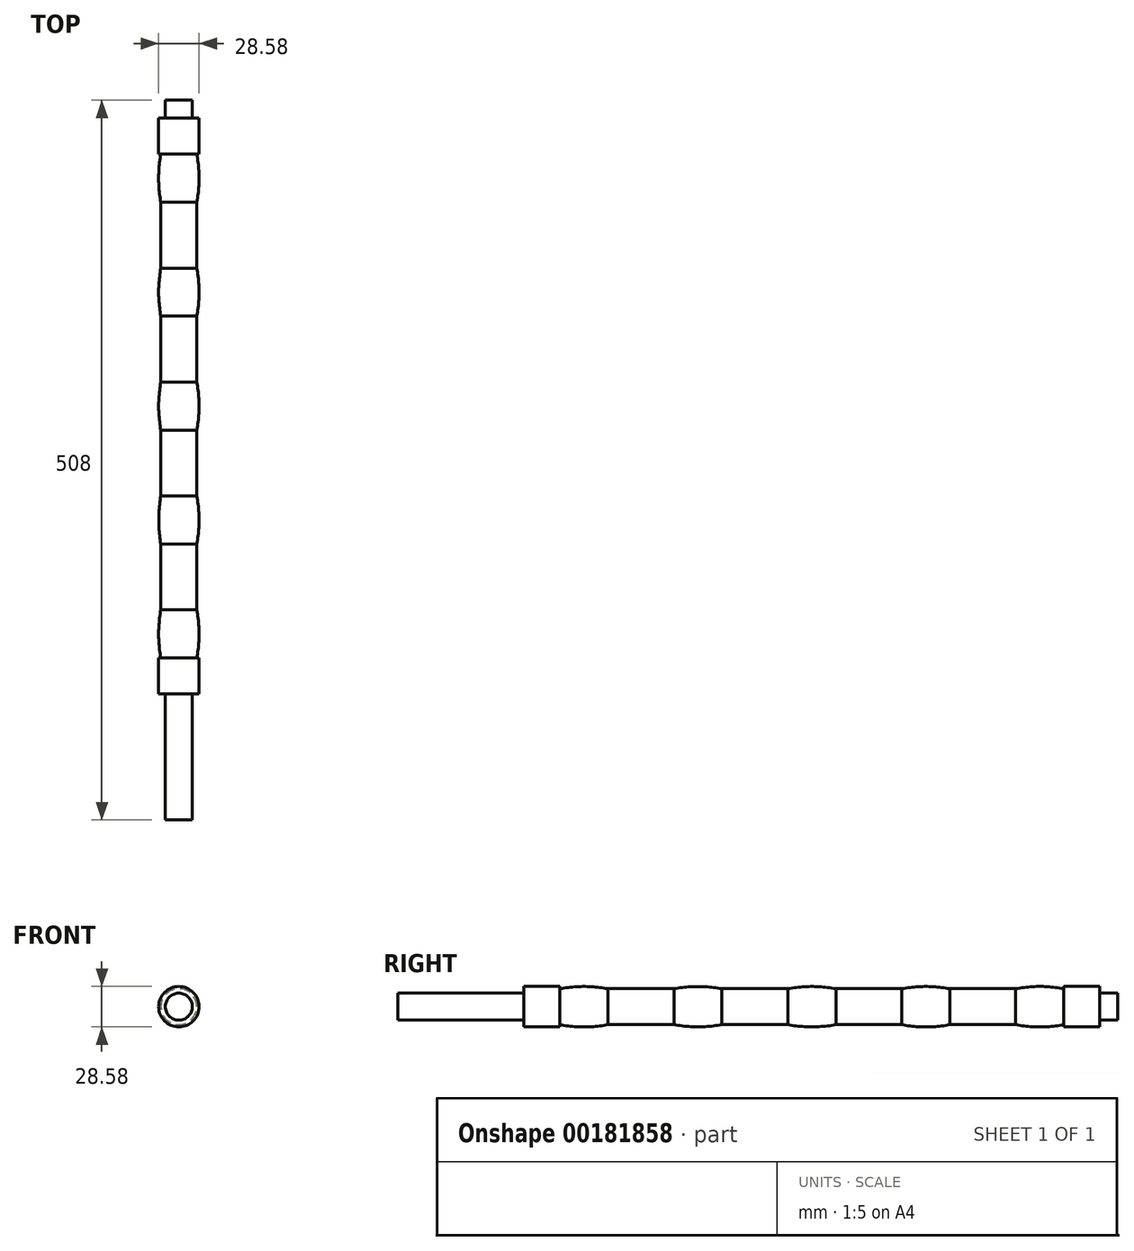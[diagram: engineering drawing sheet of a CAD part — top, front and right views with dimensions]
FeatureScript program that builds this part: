
annotation { "Feature Type Name" : "Feature", "Feature Type Description" : "" }
export const myFeature = defineFeature(function(context is Context, id is Id, definition is map)
    precondition{}
    {
        {
            var Q0;
            Q0=qCreatedBy(makeId("Front.planeOp"),FACE);
            var sketch = newSketch(context, id + "F0", { "sketchPlane" : qUnion([Q0])});
            skCircle(sketch, "E0", {"center": v(0, 0) * mm, "radius": 9.53 * mm});
            skSolve(sketch);
        }
        {
            var Q0;
            Q0 = qSketchRegion(id + "F0", true);
            extrude(context, id + "F1", {"entities" : qUnion([Q0]), "depth" : 508 * mm});
        }
        {
            var Q0;
            Q0=qCreatedBy(makeId("Right.planeOp"),FACE);
            var sketch = newSketch(context, id + "F2", { "sketchPlane" : qUnion([Q0])});
            skLineSegment(sketch, "E1", {"start": v(0, 0) * mm, "end": v(-12.7, 0) * mm});
            skLineSegment(sketch, "E2", {"start": v(-12.7, 0) * mm, "end": v(-12.7, 14.29) * mm});
            skLineSegment(sketch, "E3", {"start": v(-12.7, 14.29) * mm, "end": v(-38.1, 14.29) * mm});
            skPoint(sketch, "E4.end.orphan", {"position": v(-419.1, 0) * mm});
            skLineSegment(sketch, "E5", {"start": v(-419.1, 0) * mm, "end": v(-419.1, 14.29) * mm});
            skLineSegment(sketch, "E6", {"start": v(-419.1, 0) * mm, "end": v(-12.7, 0) * mm});
            skArc(sketch, "E7", {"start": v(-198.95, 12.69) * mm, "mid": v(-215.9, 14.25) * mm, "end": v(-232.85, 12.69) * mm});
            skLineSegment(sketch, "E8.trimOffspring", {"start": v(-232.85, 12.69) * mm, "end": v(-279.36, 12.69) * mm});
            skArc(sketch, "E9", {"start": v(-38.1, 12.69) * mm, "mid": v(-55.05, 14.27) * mm, "end": v(-72, 12.69) * mm});
            skLineSegment(sketch, "E10.trimOffspring", {"start": v(-72, 12.69) * mm, "end": v(-118.52, 12.69) * mm});
            skLineSegment(sketch, "E11", {"start": v(-38.1, 12.69) * mm, "end": v(-38.1, 14.29) * mm});
            skLineSegment(sketch, "E12", {"start": v(-198.95, 12.69) * mm, "end": v(-152.43, 12.69) * mm});
            skArc(sketch, "E13", {"start": v(-118.52, 12.69) * mm, "mid": v(-135.48, 14.25) * mm, "end": v(-152.43, 12.69) * mm});
            skLineSegment(sketch, "E14.trimOffspring", {"start": v(-152.43, 12.69) * mm, "end": v(-198.95, 12.69) * mm});
            skLineSegment(sketch, "E15", {"start": v(-419.1, 14.29) * mm, "end": v(-393.7, 14.29) * mm});
            skLineSegment(sketch, "E16", {"start": v(-393.7, 14.29) * mm, "end": v(-393.7, 12.69) * mm});
            skArc(sketch, "E17", {"start": v(-359.8, 12.69) * mm, "mid": v(-376.75, 14.27) * mm, "end": v(-393.7, 12.69) * mm});
            skLineSegment(sketch, "E18.trimOffspring", {"start": v(-393.7, 12.69) * mm, "end": v(-419.1, 12.69) * mm});
            skLineSegment(sketch, "E19", {"start": v(-359.8, 12.69) * mm, "end": v(-313.27, 12.69) * mm});
            skArc(sketch, "E20", {"start": v(-279.36, 12.69) * mm, "mid": v(-296.32, 14.2) * mm, "end": v(-313.27, 12.69) * mm});
            skLineSegment(sketch, "E21.trimOffspring", {"start": v(-313.27, 12.69) * mm, "end": v(-359.8, 12.69) * mm});
            skLineSegment(sketch, "E22.trimOffspring", {"start": v(-393.7, 14.29) * mm, "end": v(-419.1, 14.29) * mm});
            skSolve(sketch);
        }
        {
            var Q0;
            Q0 = qSketchRegion(id + "F2", true);
            var Q1;
            Q1=makeQuery(id+"F1.opExtrude","SWEPT_FACE",FACE,{"disambiguationData":[OSD([sQuery(id+"F0.wireOp",EDGE,"E0")])]});
            revolve(context, id + "F3", {"operationType" : NewBodyOperationType.ADD, "entities" : qUnion([Q0]), "axis" : qUnion([Q1]), "revolveType" : RevolveType.FULL});
        }
    });
